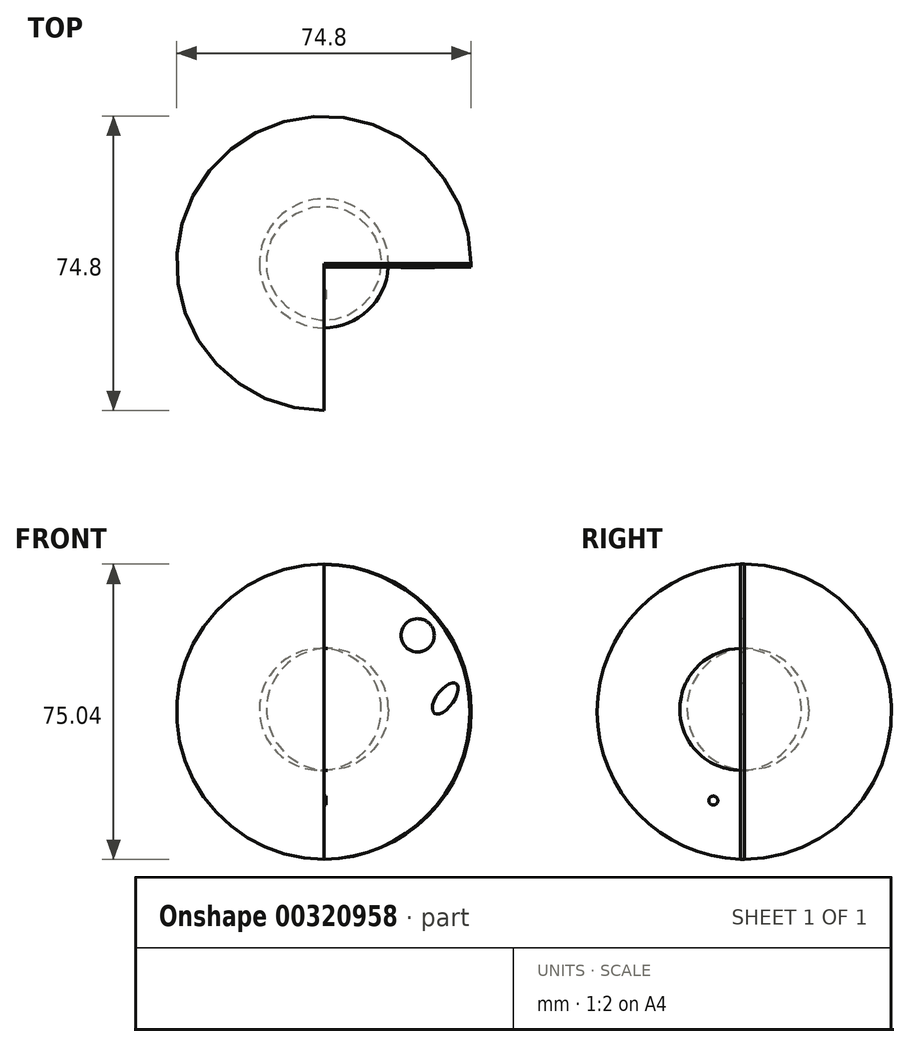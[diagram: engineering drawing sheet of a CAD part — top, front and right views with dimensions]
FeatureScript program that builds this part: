
annotation { "Feature Type Name" : "Feature", "Feature Type Description" : "" }
export const myFeature = defineFeature(function(context is Context, id is Id, definition is map)
    precondition{}
    {
        {
            var Q0;
            Q0=qCreatedBy(makeId("Front.planeOp"),FACE);
            var sketch = newSketch(context, id + "F0", { "sketchPlane" : qUnion([Q0])});
            skLineSegment(sketch, "E0", {"start": v(0, 0) * mm, "end": v(0, 75.04) * mm});
            skArc(sketch, "E1", {"start": v(0, 0) * mm, "mid": v(37.4, 37.52) * mm, "end": v(0, 75.04) * mm});
            skSolve(sketch);
        }
        {
            var Q0;
            Q0=makeQuery(id+"F0.imprint","IMPRINT",FACE,{"disambiguationData":[TD([[makeQuery(id+"F0.imprint","IMPRINT",EDGE,{"derivedFrom":sQuery(id+"F0.wireOp",EDGE,"E0")}),-1.0]])]});
            var Q1;
            Q1=sQuery(id+"F0.wireOp",EDGE,"E0");
            revolve(context, id + "F1", {"entities" : qUnion([Q0]), "axis" : qUnion([Q1]), "revolveType" : RevolveType.TWO_DIRECTIONS, "angle" : 270 * degree, "angleBack" : 359.97 * degree});
        }
        {
            var Q0;
            Q0=makeQuery(id+"F1.opRevolve","CAP_FACE",FACE,{"disambiguationData":[OSD([sQuery(id+"F0.wireOp",EDGE,"E0"),sQuery(id+"F0.wireOp",EDGE,"E1")])],"isStart":false});
            var sketch = newSketch(context, id + "F2", { "sketchPlane" : qUnion([Q0])});
            skLineSegment(sketch, "E2", {"start": v(0, 22.67) * mm, "end": v(0, 53.56) * mm});
            skArc(sketch, "E3", {"start": v(0, 22.67) * mm, "mid": v(16.38, 38.12) * mm, "end": v(0, 53.56) * mm});
            skSolve(sketch);
        }
        {
            var Q0;
            Q0 = qSketchRegion(id + "F2", true);
            var Q1;
            Q1=sQuery(id+"F2.wireOp",EDGE,"E2");
            revolve(context, id + "F3", {"entities" : qUnion([Q0]), "axis" : qUnion([Q1]), "revolveType" : RevolveType.SYMMETRIC, "angle" : 360 * degree});
        }
        {
            var Q0;
            {var subQ0=sQuery(id+"F2.wireOp",EDGE,"E2");Q0=makeQuery(id+"F2.imprint","IMPRINT",FACE,{"disambiguationData":[TD([[makeQuery(id+"F2.imprint","IMPRINT",EDGE,{"derivedFrom":subQ0}),1.0]])]});}
            var sketch = newSketch(context, id + "F4", { "sketchPlane" : qUnion([Q0])});
            skFitSpline(sketch, "E4", {"points": [v(-31, 27.47) * mm, v(-27.03, 28.47) * mm, v(-29.18, 25.15) * mm, v(-24.56, 26.4) * mm, v(-27.76, 23.36) * mm, v(-23.34, 24.2) * mm, v(-25.34, 21.22) * mm], "startDerivative": vector(38.09, 15.75) * mm, "endDerivative": vector(-26.96, -27.7) * mm});
            skSolve(sketch);
        }
        {
            var Q0;
            Q0=sQuery(id+"F4.wireOp",EDGE,"E4");
            extrude(context, id + "F5", {"bodyType" : ToolBodyType.SURFACE, "surfaceEntities" : qUnion([Q0]), "depth" : 2.54 * mm});
        }
        {
            var Q0;
            Q0 = qSketchRegion(id + "F0", true);
            var sketch = newSketch(context, id + "F6", { "sketchPlane" : qUnion([Q0])});
            skArc(sketch, "E5", {"start": v(0, 0) * mm, "mid": v(37.07, 37.47) * mm, "end": v(0, 74.94) * mm});
            skSolve(sketch);
        }
        {
            var Q0;
            {var subQ0=sQuery(id+"F6.wireOp",EDGE,"E5");Q0=makeQuery(id+"F6.imprint","IMPRINT",FACE,{"disambiguationData":[TD([[makeQuery(id+"F6.imprint","IMPRINT",EDGE,{"derivedFrom":subQ0}),-1.0]])]});}
            extrude(context, id + "F7", {"entities" : qUnion([Q0]), "depth" : 1 * mm});
        }
        {
            var Q0;
            Q0=makeQuery(id+"F0.imprint","IMPRINT",FACE,{"disambiguationData":[TD([[makeQuery(id+"F0.imprint","IMPRINT",EDGE,{"derivedFrom":sQuery(id+"F0.wireOp",EDGE,"E0")}),-1.0]])]});
            var sketch = newSketch(context, id + "F8", { "sketchPlane" : qUnion([Q0])});
            skEllipse(sketch, "E6", {"center": v(30.8, 40.9) * mm, "majorRadius": 4.67 * mm, "minorRadius": 2.18 * mm, "majorAxis": v(-0.59, -0.8)});
            skSolve(sketch);
        }
        {
            var Q0;
            Q0 = qSketchRegion(id + "F8", true);
            extrude(context, id + "F9", {"entities" : qUnion([Q0]), "depth" : 1 * mm});
        }
        {
            var Q0;
            {var subQ0=sQuery(id+"F2.wireOp",EDGE,"E2");Q0=makeQuery(id+"F2.imprint","IMPRINT",FACE,{"disambiguationData":[TD([[makeQuery(id+"F2.imprint","IMPRINT",EDGE,{"derivedFrom":subQ0}),1.0]])]});}
            var sketch = newSketch(context, id + "F10", { "sketchPlane" : qUnion([Q0])});
            skCircle(sketch, "E7", {"center": v(-7.88, 14.93) * mm, "radius": 1.15 * mm});
            skSolve(sketch);
        }
        {
            var Q0;
            Q0 = qSketchRegion(id + "F10", true);
            extrude(context, id + "F11", {"entities" : qUnion([Q0]), "depth" : 0.5 * mm});
        }
        {
            var Q0;
            {var subQ0=sQuery(id+"F2.wireOp",EDGE,"E2");Q0=makeQuery(id+"F2.imprint","IMPRINT",FACE,{"disambiguationData":[TD([[makeQuery(id+"F2.imprint","IMPRINT",EDGE,{"derivedFrom":subQ0}),1.0]])]});}
            var sketch = newSketch(context, id + "F12", { "sketchPlane" : qUnion([Q0])});
            skFitSpline(sketch, "E8", {"points": [v(-7, 52.38) * mm, v(-4.05, 55.58) * mm, v(-12.06, 51.01) * mm, v(-4.8, 58.22) * mm, v(-16.56, 50.27) * mm, v(-4.76, 61.84) * mm, v(-19.28, 52.76) * mm, v(-11.9, 61.72) * mm], "startDerivative": vector(63.99, 59.37) * mm, "endDerivative": vector(97.7, 101.01) * mm});
            skSolve(sketch);
        }
        {
            var Q0;
            Q0=sQuery(id+"F12.wireOp",EDGE,"E8");
            extrude(context, id + "F13", {"bodyType" : ToolBodyType.SURFACE, "surfaceEntities" : qUnion([Q0]), "depth" : 1 * mm});
        }
        {
            var Q0;
            Q0=makeQuery(id+"F0.imprint","IMPRINT",FACE,{"disambiguationData":[TD([[makeQuery(id+"F0.imprint","IMPRINT",EDGE,{"derivedFrom":sQuery(id+"F0.wireOp",EDGE,"E0")}),-1.0]])]});
            var sketch = newSketch(context, id + "F14", { "sketchPlane" : qUnion([Q0])});
            skFitSpline(sketch, "E9", {"points": [v(3.82, 22.38) * mm, v(17.45, 25.1) * mm, v(3.86, 19.85) * mm, v(23.42, 23.9) * mm, v(5.73, 18.31) * mm, v(19.26, 20.26) * mm, v(11.6, 17.04) * mm], "startDerivative": vector(143.83, 34.1) * mm, "endDerivative": vector(-109.33, -38.04) * mm});
            skSolve(sketch);
        }
        {
            var Q0;
            Q0=sQuery(id+"F14.wireOp",EDGE,"E9");
            extrude(context, id + "F15", {"bodyType" : ToolBodyType.SURFACE, "surfaceEntities" : qUnion([Q0]), "depth" : 1 * mm});
        }
        {
            var Q0;
            Q0=makeQuery(id+"F1.opRevolve","CAP_FACE",FACE,{"disambiguationData":[OSD([sQuery(id+"F0.wireOp",EDGE,"E0"),sQuery(id+"F0.wireOp",EDGE,"E1")])],"isStart":true});
            var sketch = newSketch(context, id + "F16", { "sketchPlane" : qUnion([Q0])});
            skCircle(sketch, "E10", {"center": v(23.8, 56.93) * mm, "radius": 4.23 * mm});
            skSolve(sketch);
        }
        {
            var Q0;
            Q0 = qSketchRegion(id + "F16", true);
            extrude(context, id + "F17", {"entities" : qUnion([Q0]), "depth" : 1 * mm});
        }
    });
